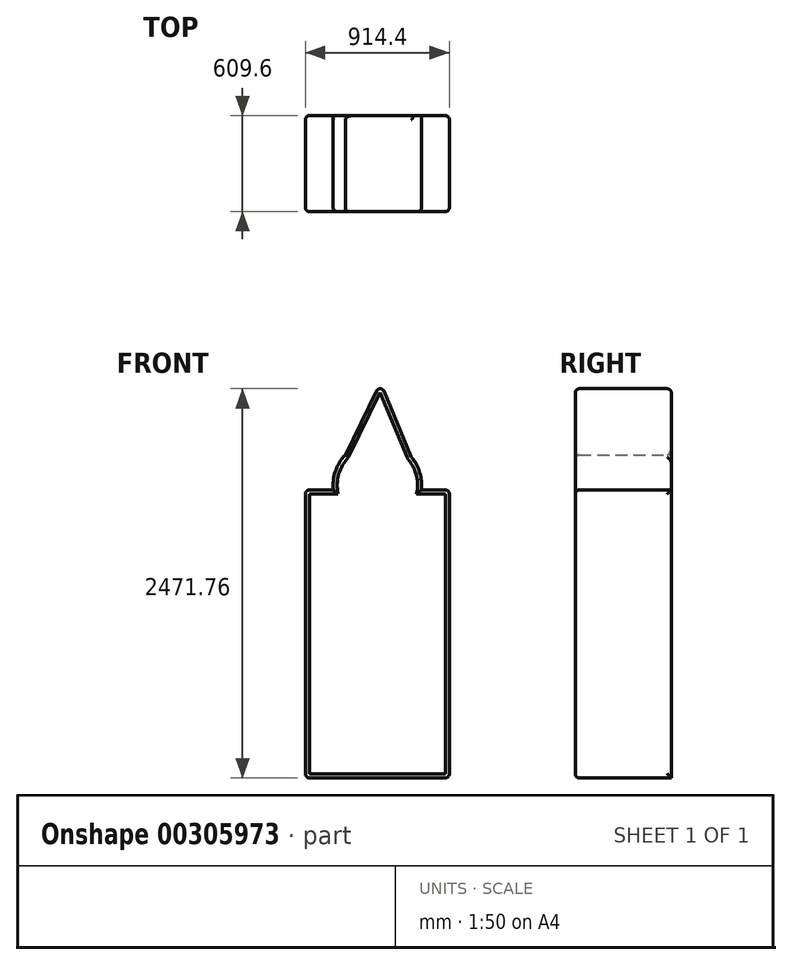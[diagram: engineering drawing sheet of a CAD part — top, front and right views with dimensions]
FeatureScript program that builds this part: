
annotation { "Feature Type Name" : "Feature", "Feature Type Description" : "" }
export const myFeature = defineFeature(function(context is Context, id is Id, definition is map)
    precondition{}
    {
        {
            var Q0;
            Q0=qCreatedBy(makeId("Front.planeOp"),FACE);
            var sketch = newSketch(context, id + "F0", { "sketchPlane" : qUnion([Q0])});
            skLineSegment(sketch, "E0", {"start": v(-50.94, 906.92) * mm, "end": v(-50.94, -921.88) * mm});
            skLineSegment(sketch, "E1", {"start": v(-50.94, -921.88) * mm, "end": v(863.46, -921.88) * mm});
            skLineSegment(sketch, "E2", {"start": v(863.46, -921.88) * mm, "end": v(863.46, 906.92) * mm});
            skLineSegment(sketch, "E3", {"start": v(-50.94, 906.92) * mm, "end": v(126.86, 906.92) * mm});
            skLineSegment(sketch, "E4", {"start": v(863.46, 906.92) * mm, "end": v(685.66, 906.92) * mm});
            skArc(sketch, "E5", {"start": v(685.66, 906.92) * mm, "mid": v(406.26, 1217.5) * mm, "end": v(126.86, 906.92) * mm});
            skLineSegment(sketch, "E6", {"start": v(202.45, 1129.93) * mm, "end": v(426.19, 1586) * mm});
            skLineSegment(sketch, "E7", {"start": v(426.19, 1586) * mm, "end": v(621.54, 1117.07) * mm});
            skSolve(sketch);
        }
        {
            var Q0;
            Q0=makeQuery(id+"F0.imprint","IMPRINT",FACE,{"disambiguationData":[TD([[makeQuery(id+"F0.imprint","IMPRINT",EDGE,{"derivedFrom":sQuery(id+"F0.wireOp",EDGE,"E0")}),1.0]])]});
            var Q1;
            {var subQ0=sQuery(id+"F0.wireOp",EDGE,"E6");Q1=makeQuery(id+"F0.imprint","IMPRINT",FACE,{"disambiguationData":[TD([[makeQuery(id+"F0.imprint","IMPRINT",EDGE,{"derivedFrom":subQ0}),-1.0]])]});}
            extrude(context, id + "F1", {"entities" : qUnion([Q0, Q1]), "depth" : 609.6 * mm});
        }
        {
            var Q0;
            Q0=makeQuery(id+"F1.opExtrude","CAP_EDGE",EDGE,{"disambiguationData":[OSD([sQuery(id+"F0.wireOp",EDGE,"E7")])],"isStart":false});
            var Q1;
            Q1=makeQuery(id+"F1.opExtrude","CAP_FACE",FACE,{"disambiguationData":[OSD([sQuery(id+"F0.wireOp",EDGE,"E0"),sQuery(id+"F0.wireOp",EDGE,"E1"),sQuery(id+"F0.wireOp",EDGE,"E2"),sQuery(id+"F0.wireOp",EDGE,"E3"),sQuery(id+"F0.wireOp",EDGE,"E4"),sQuery(id+"F0.wireOp",EDGE,"E5"),sQuery(id+"F0.wireOp",EDGE,"E6"),sQuery(id+"F0.wireOp",EDGE,"E7")])],"isStart":false});
            var Q2;
            Q2=makeQuery(id+"F1.opExtrude","CAP_EDGE",EDGE,{"disambiguationData":[OSD([sQuery(id+"F0.wireOp",EDGE,"E7")])],"isStart":true});
            var Q3;
            Q3=makeQuery(id+"F1.opExtrude","SWEPT_FACE",FACE,{"disambiguationData":[OSD([sQuery(id+"F0.wireOp",EDGE,"E7")])]});
            var Q4;
            Q4=makeQuery(id+"F1.opExtrude","SWEPT_EDGE",EDGE,{"disambiguationData":[OSD([sQuery(id+"F0.wireOp",EDGE,"E2"),sQuery(id+"F0.wireOp",EDGE,"E4")])]});
            var Q5;
            Q5=makeQuery(id+"F1.opExtrude","SWEPT_FACE",FACE,{"disambiguationData":[OSD([sQuery(id+"F0.wireOp",EDGE,"E2")])]});
            var Q6;
            Q6=makeQuery(id+"F1.opExtrude","SWEPT_EDGE",EDGE,{"disambiguationData":[OSD([sQuery(id+"F0.wireOp",EDGE,"E0"),sQuery(id+"F0.wireOp",EDGE,"E3")])]});
            var Q7;
            Q7=makeQuery(id+"F1.opExtrude","SWEPT_FACE",FACE,{"disambiguationData":[OSD([sQuery(id+"F0.wireOp",EDGE,"E0")])]});
            var Q8;
            Q8=makeQuery(id+"F1.opExtrude","CAP_EDGE",EDGE,{"disambiguationData":[OSD([sQuery(id+"F0.wireOp",EDGE,"E6")])],"isStart":true});
            var Q9;
            Q9=makeQuery(id+"F1.opExtrude","CAP_EDGE",EDGE,{"disambiguationData":[OSD([sQuery(id+"F0.wireOp",EDGE,"E3")])],"isStart":true});
            fillet(context, id + "F2", {"entities" : qUnion([Q0, Q1, Q2, Q3, Q4, Q5, Q6, Q7, Q8, Q9]), "radius" : 25.4 * mm, "tangentPropagation" : true, "allowEdgeOverflow" : false});
        }
        {
            var Q0;
            Q0=makeQuery(id+"F1.opExtrude","CAP_FACE",FACE,{"disambiguationData":[OSD([sQuery(id+"F0.wireOp",EDGE,"E0"),sQuery(id+"F0.wireOp",EDGE,"E1"),sQuery(id+"F0.wireOp",EDGE,"E2"),sQuery(id+"F0.wireOp",EDGE,"E3"),sQuery(id+"F0.wireOp",EDGE,"E4"),sQuery(id+"F0.wireOp",EDGE,"E5"),sQuery(id+"F0.wireOp",EDGE,"E6"),sQuery(id+"F0.wireOp",EDGE,"E7")])],"isStart":false});
            shell(context, id + "F3", {"entities" : qUnion([Q0]), "thickness" : 2.54 * mm});
        }
    });
